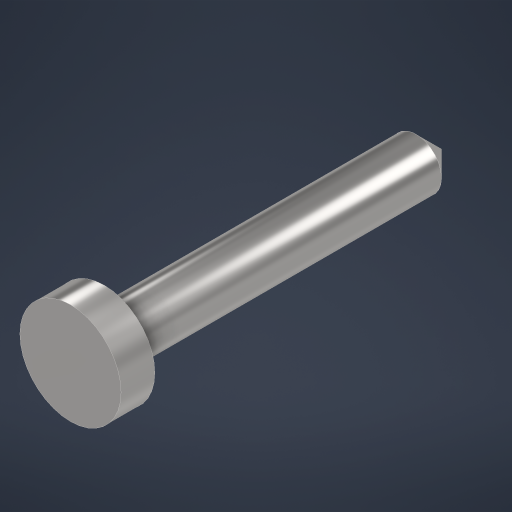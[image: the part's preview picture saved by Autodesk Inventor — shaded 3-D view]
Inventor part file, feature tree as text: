
AUTODESK INVENTOR PART (.ipt)
format: ipt  version: 2023.2 (Build 272271000, 271)  size: 239,104 bytes
history: native  units: mm
features: revolve x1
ambient origin geometry x8: Origin, YZ Plane, XZ Plane, XY Plane, X Axis, Y Axis, Z Axis, Center Point
bodies: Body1 (feature_tree)
feature tree (1):
  revolve  "Revolution1"  [1 undecoded]
note: 1 required parameter value undecoded (feature->parameter linkage not recoverable at this tier; creation-order binding heuristic only, values carry confidence <= 0.55)
